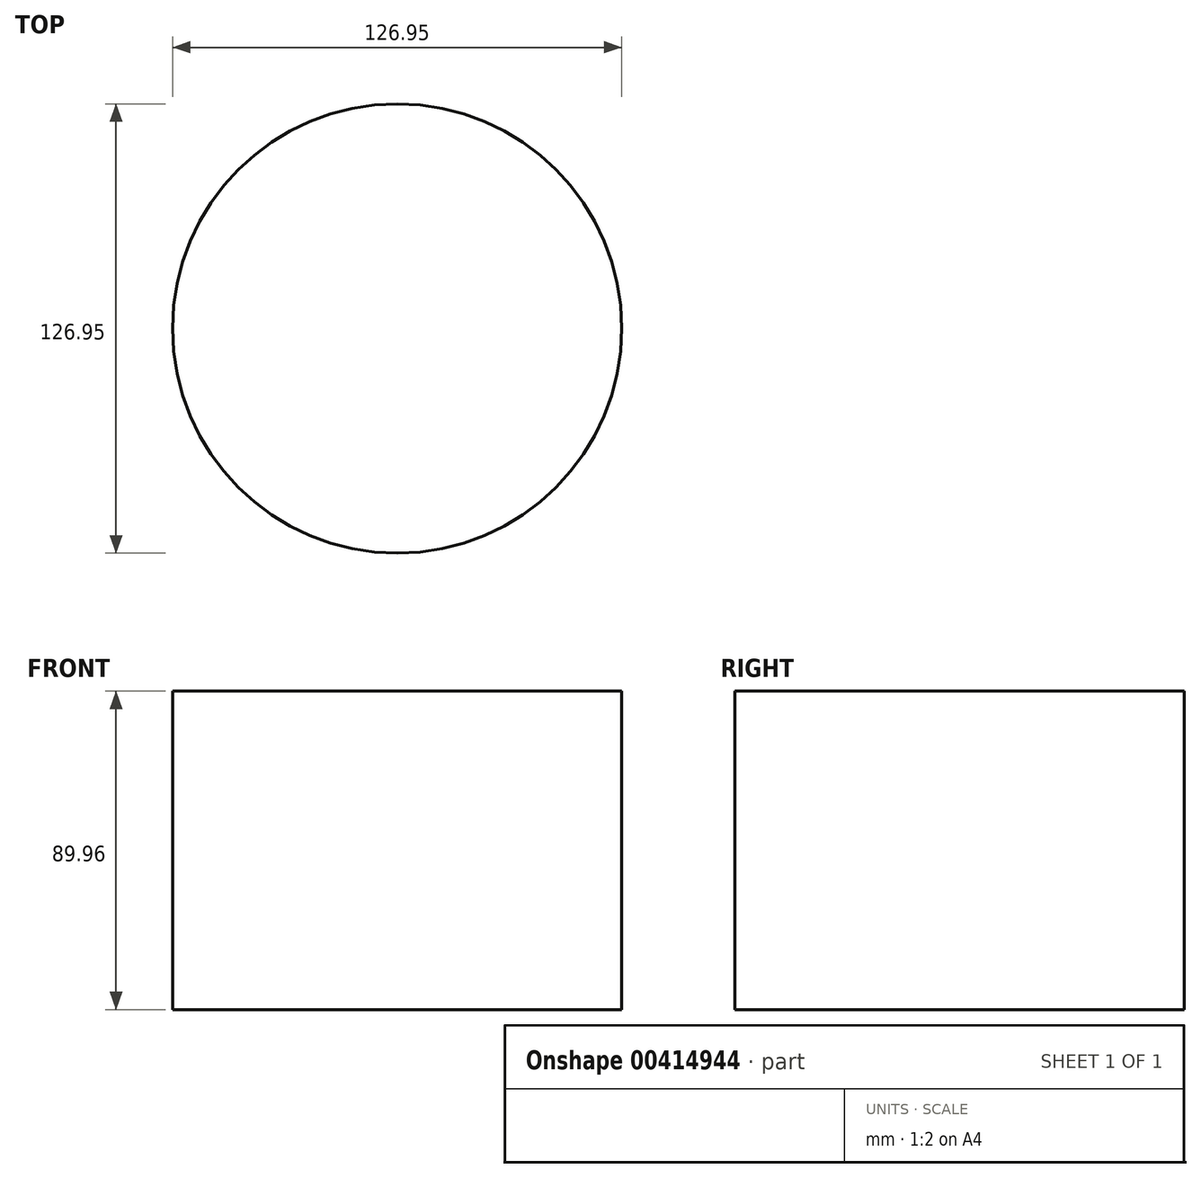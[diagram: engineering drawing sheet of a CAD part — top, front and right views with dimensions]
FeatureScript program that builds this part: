
annotation { "Feature Type Name" : "Feature", "Feature Type Description" : "" }
export const myFeature = defineFeature(function(context is Context, id is Id, definition is map)
    precondition{}
    {
        {
            var Q0;
            Q0=qCreatedBy(makeId("Top.planeOp"),FACE);
            var sketch = newSketch(context, id + "F0", { "sketchPlane" : qUnion([Q0])});
            skCircle(sketch, "E0", {"center": v(-13.78, -16.67) * mm, "radius": 21.63 * mm});
            skCircle(sketch, "E1", {"center": v(8.56, 6) * mm, "radius": 53.46 * mm});
            skCircle(sketch, "E2", {"center": v(10.65, -47.41) * mm, "radius": 63.47 * mm});
            skSolve(sketch);
        }
        {
            var Q0;
            Q0=sQuery(id+"F0.wireOp",EDGE,"E2");
            extrude(context, id + "F1", {"bodyType" : ToolBodyType.SURFACE, "surfaceEntities" : qUnion([Q0]), "depth" : 89.96 * mm});
        }
    });
